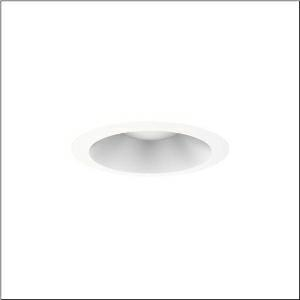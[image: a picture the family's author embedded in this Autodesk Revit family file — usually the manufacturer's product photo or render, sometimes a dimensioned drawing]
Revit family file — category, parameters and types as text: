
# Revit family: lunis_31-xl_51dn15eg32b
name_source: partatom
category: Lighting Fixtures
units: mm (PartAtom-declared; Revit-internal decimal feet)

## family parameters
Cut with Voids When Loaded = No
Host = Face
Light Source = No
Part Type = Normal
Room Calculation Point = No
Round Connector Dimension = Use Diameter
Shared = No

## types (1)
- --- (1 x LED, 2380 lm, 17.5 W, 3000K)
    Apparent Load = 18 VA
    CIE Flux Codes = 89 99 100 100 100
    Color Rendering = 80
    Color Temperature = 3000K
    Default Elevation = 1800 mm
    Description = Lunis 31, -XL, downlight, light control with lens, light emission: direct distribution, LED rated luminous flux: 2.380lm, light colour: 830, mains connection: 220..240V, AC, 50/60Hz, housing, of aluminium, white, protection rating (complete): IP20, protection rating (on room side): IP54, insulation class (complete): insulation class II (safety insulation), certification: CE, packaging unit: 1 piece
    Height = 0 mm  [stored 0 ft]
    Lamp = 1 x LED
    Lamp Light Flux = 2380 lm
    Lamp Power = 17.5 W
    Lamp count = 1
    Length = 259 mm
    Luminous efficacy = 136 lm/W
    Manufacturer = Siteco
    ModVariant = No
    Model = 51DN15EG32B
    Mounting Place = Ceiling
    Mounting Type = Recessed
    Number of Poles = 1
    OnlyDefault = Yes
    Power Factor = 1
    Product Name = Lunis 31-XL
    Product group = downlight
    ProductGroupID = 400
    Protection Class = Protection class II
    Protection Degree = IP 20
    RLX_Detail_Level = 1
    RLX_Emergency_Light_Flux = 0 lm
    RLX_Emergency_Type = 0
    RLX_Emergency_Type_DB = No
    RlxData = <blob elided: 24173 chars, md5=40dcc527>
    Socket = socket
    Standby Power = 0 W
    System Light Flux = 2380 lm
    System Power = 18 W
    Type Comments = individual setting: luminous flux: 100 % | (ON | OFF | ON) | 450 mA
    Type Image = l_1345915.jpg
    URL = http://relux.com
    VarID = @adj_010075
    Voltage = 0 V
    Weight = 0.00 kg
    Width = 0 mm  [stored 0 ft]

note: [stored X ft] marks values corroborated as IEEE doubles in the binary element streams (Revit-internal decimal feet)

## geometry (parser evidence)
native form markers: Blend x4, Sweep x11
no freeform markers — native parametric forms only
